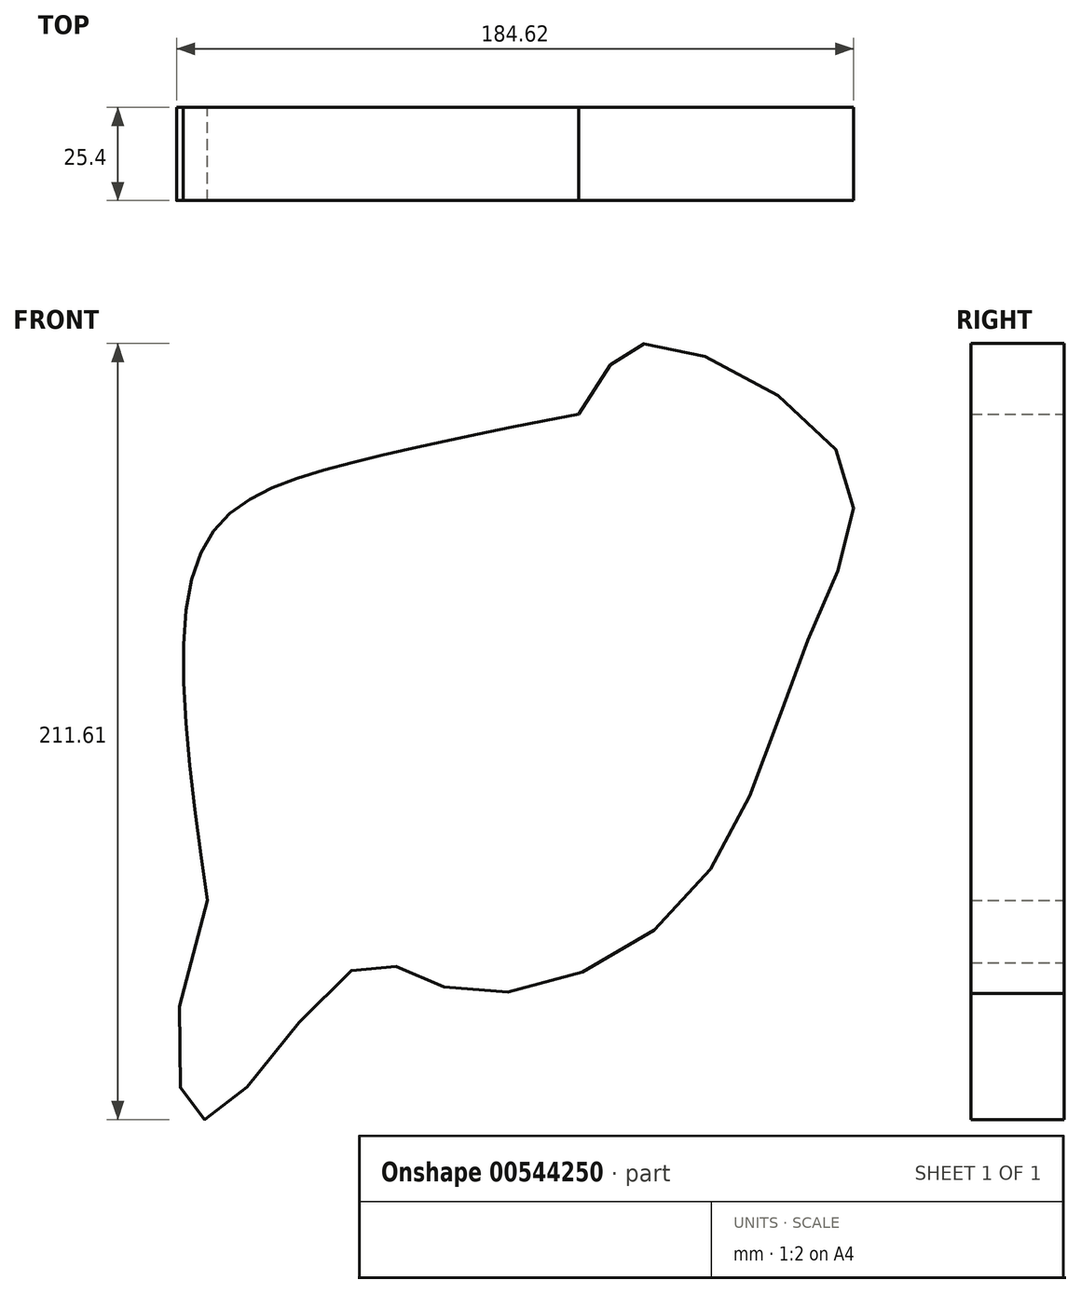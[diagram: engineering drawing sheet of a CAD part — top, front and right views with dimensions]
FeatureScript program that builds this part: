
annotation { "Feature Type Name" : "Feature", "Feature Type Description" : "" }
export const myFeature = defineFeature(function(context is Context, id is Id, definition is map)
    precondition{}
    {
        {
            var Q0;
            Q0=qCreatedBy(makeId("Front.planeOp"),FACE);
            var sketch = newSketch(context, id + "F0", { "sketchPlane" : qUnion([Q0])});
            skFitSpline(sketch, "E0", {"points": [v(0, 61.96) * mm, v(-68.3, 47) * mm, v(-102.4, 25.43) * mm, v(-101.25, -70.67) * mm], "startDerivative": vector(-212.8, -41.33) * mm, "endDerivative": vector(40.81, -287.42) * mm});
            skFitSpline(sketch, "E1", {"points": [v(-60.66, -88.98) * mm, v(-33.6, -95.13) * mm, v(27.69, -72.36) * mm, v(62.36, 0) * mm, v(72.08, 49.16) * mm, v(18.44, 81.2) * mm, v(0, 61.96) * mm, v(-101.25, -70.67) * mm, v(-101.25, -130.32) * mm, v(-60.66, -88.98) * mm]});
            skSolve(sketch);
        }
        {
            var Q0;
            Q0 = qSketchRegion(id + "F0", true);
            extrude(context, id + "F1", {"entities" : qUnion([Q0]), "depth" : 25.4 * mm, "offsetDistance" : 25.4 * mm});
        }
    });
